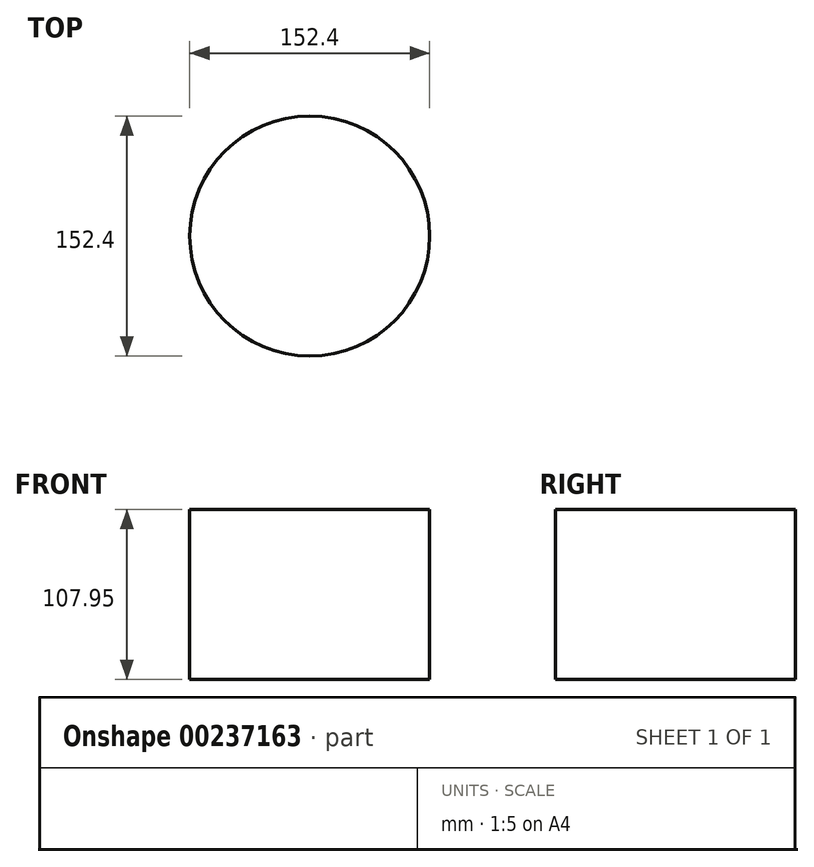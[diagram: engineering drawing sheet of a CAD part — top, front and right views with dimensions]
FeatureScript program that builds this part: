
annotation { "Feature Type Name" : "Feature", "Feature Type Description" : "" }
export const myFeature = defineFeature(function(context is Context, id is Id, definition is map)
    precondition{}
    {
        {
            var Q0;
            Q0=qCreatedBy(makeId("Top.planeOp"),FACE);
            var sketch = newSketch(context, id + "F0", { "sketchPlane" : qUnion([Q0])});
            skCircle(sketch, "E0", {"center": v(0, 0) * mm, "radius": 76.2 * mm});
            skSolve(sketch);
        }
        {
            var Q0;
            Q0=makeQuery(id+"F0.imprint","IMPRINT",FACE,{"disambiguationData":[TD([[makeQuery(id+"F0.imprint","IMPRINT",EDGE,{"derivedFrom":sQuery(id+"F0.wireOp",EDGE,"E0")}),1.0]])]});
            extrude(context, id + "F1", {"entities" : qUnion([Q0]), "depth" : 107.95 * mm});
        }
    });
